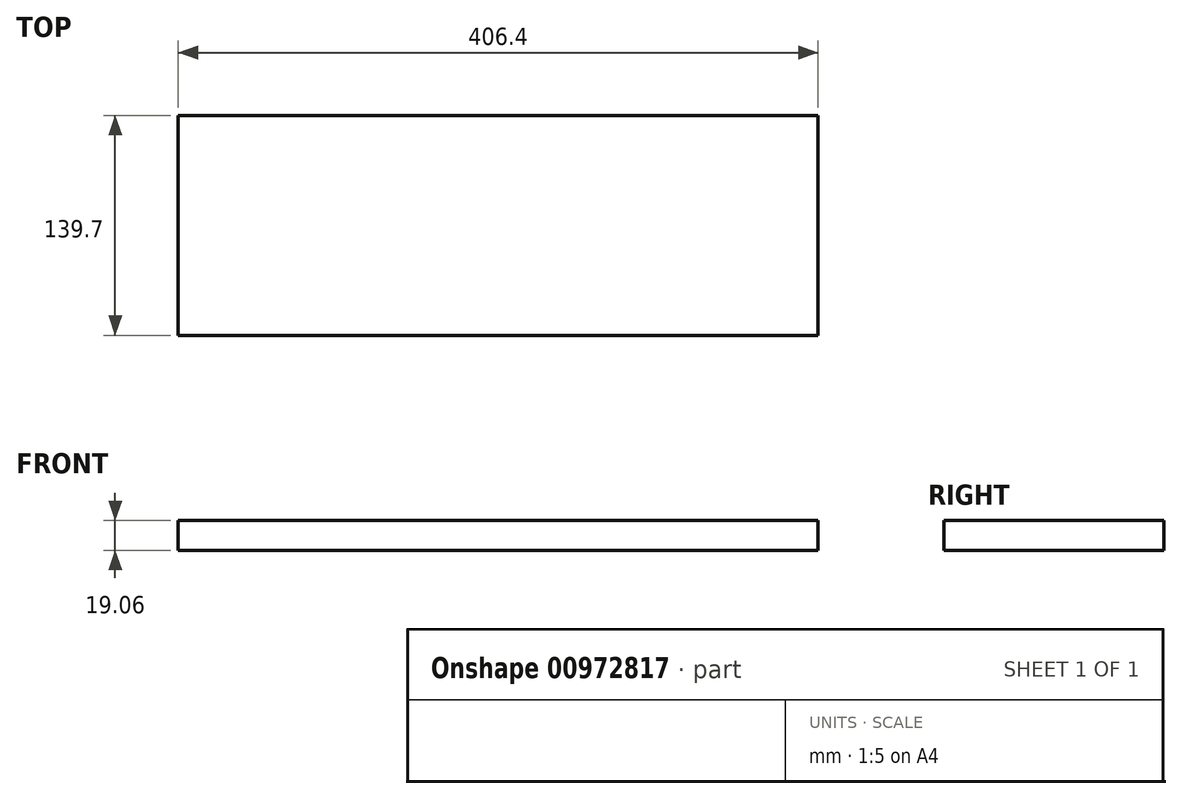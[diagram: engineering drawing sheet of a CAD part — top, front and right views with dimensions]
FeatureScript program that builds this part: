
annotation { "Feature Type Name" : "Feature", "Feature Type Description" : "" }
export const myFeature = defineFeature(function(context is Context, id is Id, definition is map)
    precondition{}
    {
        {
            var Q0;
            Q0=qCreatedBy(makeId("Right.planeOp"),FACE);
            var sketch = newSketch(context, id + "F0", { "sketchPlane" : qUnion([Q0])});
            skLineSegment(sketch, "E0.bottom", {"start": v(69.85, 9.53) * mm, "end": v(-69.85, 9.53) * mm});
            skLineSegment(sketch, "E0.top", {"start": v(69.85, -9.53) * mm, "end": v(-69.85, -9.53) * mm});
            skLineSegment(sketch, "E0.left", {"start": v(69.85, 9.53) * mm, "end": v(69.85, -9.53) * mm});
            skLineSegment(sketch, "E0.right", {"start": v(-69.85, 9.53) * mm, "end": v(-69.85, -9.53) * mm});
            skPoint(sketch, "E0.middle", {"position": v(0, 0) * mm});
            skSolve(sketch);
        }
        {
            var Q0;
            Q0=makeQuery(id+"F0.imprint","IMPRINT",FACE,{"disambiguationData":[TD([[makeQuery(id+"F0.imprint","IMPRINT",EDGE,{"derivedFrom":sQuery(id+"F0.wireOp",EDGE,"E0.bottom")}),1.0]])]});
            extrude(context, id + "F1", {"entities" : qUnion([Q0]), "depth" : 406.4 * mm, "offsetDistance" : 25.4 * mm});
        }
    });
